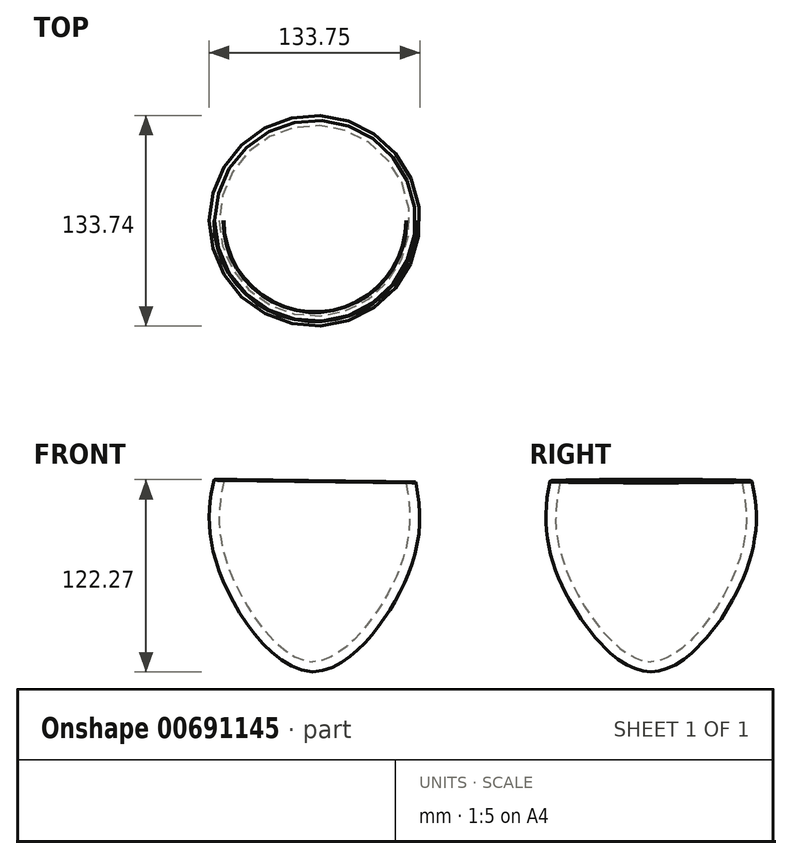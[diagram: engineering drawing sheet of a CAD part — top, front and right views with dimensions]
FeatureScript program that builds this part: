
annotation { "Feature Type Name" : "Feature", "Feature Type Description" : "" }
export const myFeature = defineFeature(function(context is Context, id is Id, definition is map)
    precondition{}
    {
        {
            var Q0;
            Q0=qCreatedBy(makeId("Front.planeOp"),FACE);
            var sketch = newSketch(context, id + "F0", { "sketchPlane" : qUnion([Q0])});
            skFitSpline(sketch, "E0", {"points": [v(-62.57, 51.72) * mm, v(-65.55, 23.74) * mm, v(-51.22, -24.24) * mm, v(0, -70.55) * mm, v(58.39, -26.57) * mm, v(65.73, 51.72) * mm], "startDerivative": vector(-36.91, -184.64) * mm, "endDerivative": vector(-30.55, 348.97) * mm});
            skLineSegment(sketch, "E1", {"start": v(-62.57, 51.72) * mm, "end": v(65.73, 51.72) * mm});
            skLineSegment(sketch, "E2", {"start": v(1.58, 51.72) * mm, "end": v(0, -70.55) * mm});
            skSolve(sketch);
        }
        {
            var Q0;
            {var subQ3=sQuery(id+"F0.wireOp",EDGE,"E2");Q0=makeQuery(id+"F0.imprint","IMPRINT",FACE,{"disambiguationData":[TD([[makeQuery(id+"F0.imprint","IMPRINT",EDGE,{"derivedFrom":subQ3}),-1.0]])]});}
            var Q1;
            Q1=sQuery(id+"F0.wireOp",EDGE,"E2");
            revolve(context, id + "F1", {"entities" : qUnion([Q0]), "axis" : qUnion([Q1]), "revolveType" : RevolveType.FULL});
        }
        {
            var Q0;
            Q0=makeQuery(id+"F1.opRevolve","SWEPT_FACE",FACE,{"disambiguationData":[OSD([sQuery(id+"F0.wireOp",EDGE,"E1")])]});
            shell(context, id + "F2", {"entities" : qUnion([Q0]), "thickness" : 6.35 * mm});
        }
        {
            var Q0;
            Q0=makeQuery(id+"F2.opShell","OFFSET_EDGE",EDGE,{"disambiguationData":[OSD([sQuery(id+"F0.wireOp",EDGE,"E0"),sQuery(id+"F0.wireOp",EDGE,"E1")])]});
            var Q1;
            Q1=makeQuery(id+"F1.opRevolve","SWEPT_EDGE",EDGE,{"disambiguationData":[OSD([sQuery(id+"F0.wireOp",EDGE,"E0"),sQuery(id+"F0.wireOp",EDGE,"E1")])]});
            chamfer(context, id + "F3", {"entities" : qUnion([Q0, Q1]), "width" : 0.5 * mm, "tangentPropagation" : true});
        }
    });
